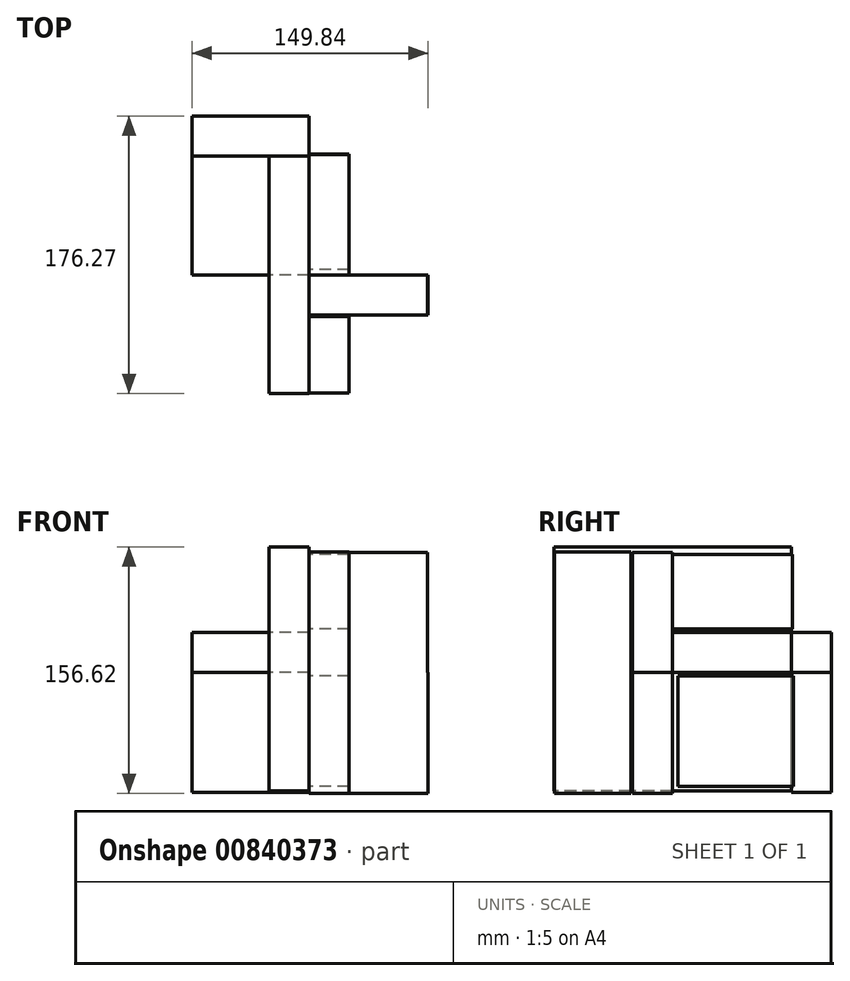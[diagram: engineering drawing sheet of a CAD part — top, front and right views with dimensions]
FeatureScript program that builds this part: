
annotation { "Feature Type Name" : "Feature", "Feature Type Description" : "" }
export const myFeature = defineFeature(function(context is Context, id is Id, definition is map)
    precondition{}
    {
        {
            var Q0;
            Q0=qCreatedBy(makeId("Top.planeOp"),FACE);
            var sketch = newSketch(context, id + "F0", { "sketchPlane" : qUnion([Q0])});
            skLineSegment(sketch, "E0.bottom", {"start": v(0, 0) * mm, "end": v(-74.45, 0) * mm});
            skLineSegment(sketch, "E0.top", {"start": v(0, 75.65) * mm, "end": v(-74.45, 75.65) * mm});
            skLineSegment(sketch, "E0.left", {"start": v(0, 0) * mm, "end": v(0, 75.65) * mm});
            skLineSegment(sketch, "E0.right", {"start": v(-74.45, 0) * mm, "end": v(-74.45, 75.65) * mm});
            skSolve(sketch);
        }
        {
            var Q0;
            Q0=makeQuery(id+"F0.imprint","IMPRINT",FACE,{"disambiguationData":[TD([[makeQuery(id+"F0.imprint","IMPRINT",EDGE,{"derivedFrom":sQuery(id+"F0.wireOp",EDGE,"E0.bottom")}),-1.0]])]});
            extrude(context, id + "F1", {"entities" : qUnion([Q0]), "depth" : 25.4 * mm, "offsetDistance" : 25.4 * mm});
        }
        {
            var Q0;
            Q0=makeQuery(id+"F1.opExtrude","SWEPT_FACE",FACE,{"disambiguationData":[OSD([sQuery(id+"F0.wireOp",EDGE,"E0.top")])]});
            var sketch = newSketch(context, id + "F2", { "sketchPlane" : qUnion([Q0])});
            skSolve(sketch);
        }
        {
            var Q0;
            Q0=makeQuery(id+"F1.opExtrude","SWEPT_FACE",FACE,{"disambiguationData":[OSD([sQuery(id+"F0.wireOp",EDGE,"E0.top")])]});
            var sketch = newSketch(context, id + "F3", { "sketchPlane" : qUnion([Q0])});
            skLineSegment(sketch, "E1.bottom", {"start": v(0, -76.29) * mm, "end": v(74.45, -76.29) * mm});
            skLineSegment(sketch, "E1.top", {"start": v(0, 0) * mm, "end": v(74.45, 0) * mm});
            skLineSegment(sketch, "E1.left", {"start": v(0, -76.29) * mm, "end": v(0, 0) * mm});
            skLineSegment(sketch, "E1.right", {"start": v(74.45, -76.29) * mm, "end": v(74.45, 0) * mm});
            skSolve(sketch);
        }
        {
            var Q0;
            Q0 = qSketchRegion(id + "F3", true);
            extrude(context, id + "F4", {"entities" : qUnion([Q0]), "depth" : 25.4 * mm, "offsetDistance" : 25.4 * mm});
        }
        {
            var Q0;
            {var subQ0=sQuery(id+"F0.wireOp",EDGE,"E0.top");Q0=makeQuery(id+"F2.imprint","IMPRINT",FACE,{"disambiguationData":[TD([[makeQuery(id+"F2.imprint","IMPRINT",EDGE,{"derivedFrom":makeQuery(id+"F1.opExtrude","CAP_EDGE",EDGE,{"disambiguationData":[OSD([subQ0])],"isStart":true})}),1.0]])]});}
            var Q1;
            Q1 = qSketchRegion(id + "F2", true);
            var Q2;
            Q2 = qSketchRegion(id + "F3", true);
            extrude(context, id + "F5", {"entities" : qUnion([Q0, Q1, Q2]), "depth" : 25.4 * mm, "offsetDistance" : 25.4 * mm});
        }
        {
            var Q0;
            Q0=qCreatedBy(makeId("Front.planeOp"),FACE);
            var sketch = newSketch(context, id + "F6", { "sketchPlane" : qUnion([Q0])});
            skLineSegment(sketch, "E2.bottom", {"start": v(0, 0) * mm, "end": v(75.4, 0) * mm});
            skLineSegment(sketch, "E2.top", {"start": v(0, -76.94) * mm, "end": v(75.4, -76.94) * mm});
            skLineSegment(sketch, "E2.left", {"start": v(0, 0) * mm, "end": v(0, -76.94) * mm});
            skLineSegment(sketch, "E2.right", {"start": v(75.4, 0) * mm, "end": v(75.4, -76.94) * mm});
            skLineSegment(sketch, "E3.bottom", {"start": v(0, 0) * mm, "end": v(75.09, 0) * mm});
            skLineSegment(sketch, "E3.top", {"start": v(0, 76.25) * mm, "end": v(75.09, 76.25) * mm});
            skLineSegment(sketch, "E3.left", {"start": v(0, 0) * mm, "end": v(0, 76.25) * mm});
            skLineSegment(sketch, "E3.right", {"start": v(75.09, 0) * mm, "end": v(75.09, 76.25) * mm});
            skSolve(sketch);
        }
        {
            var Q0;
            Q0 = qSketchRegion(id + "F6", true);
            extrude(context, id + "F7", {"entities" : qUnion([Q0]), "depth" : 25.4 * mm, "offsetDistance" : 25.4 * mm});
        }
        {
            var Q0;
            Q0=qCreatedBy(makeId("Right.planeOp"),FACE);
            var sketch = newSketch(context, id + "F8", { "sketchPlane" : qUnion([Q0])});
            skLineSegment(sketch, "E4.bottom", {"start": v(-74.8, 76.6) * mm, "end": v(-26.43, 76.6) * mm});
            skLineSegment(sketch, "E4.top", {"start": v(-74.8, -76.69) * mm, "end": v(-26.43, -76.69) * mm});
            skLineSegment(sketch, "E4.left", {"start": v(-74.8, 76.6) * mm, "end": v(-74.8, -76.69) * mm});
            skLineSegment(sketch, "E4.right", {"start": v(-26.43, 76.6) * mm, "end": v(-26.43, -76.69) * mm});
            skLineSegment(sketch, "E5.bottom", {"start": v(0, 74.79) * mm, "end": v(76.37, 74.79) * mm});
            skLineSegment(sketch, "E5.top", {"start": v(0, 27.62) * mm, "end": v(76.37, 27.62) * mm});
            skLineSegment(sketch, "E5.left", {"start": v(0, 74.79) * mm, "end": v(0, 27.62) * mm});
            skLineSegment(sketch, "E5.right", {"start": v(76.37, 74.79) * mm, "end": v(76.37, 27.62) * mm});
            skLineSegment(sketch, "E6.bottom", {"start": v(3.5, -2.3) * mm, "end": v(76.98, -2.3) * mm});
            skLineSegment(sketch, "E6.top", {"start": v(3.5, -72.45) * mm, "end": v(76.98, -72.45) * mm});
            skLineSegment(sketch, "E6.left", {"start": v(3.5, -2.3) * mm, "end": v(3.5, -72.45) * mm});
            skLineSegment(sketch, "E6.right", {"start": v(76.98, -2.3) * mm, "end": v(76.98, -72.45) * mm});
            skSolve(sketch);
        }
        {
            var Q0;
            Q0 = qSketchRegion(id + "F8", true);
            extrude(context, id + "F9", {"entities" : qUnion([Q0]), "depth" : 25.4 * mm, "offsetDistance" : 25.4 * mm});
        }
        {
            var Q0;
            Q0=makeQuery(id+"F9.opExtrude","CAP_FACE",FACE,{"disambiguationData":[OSD([sQuery(id+"F8.wireOp",EDGE,"E5.bottom"),sQuery(id+"F8.wireOp",EDGE,"E5.top"),sQuery(id+"F8.wireOp",EDGE,"E5.left"),sQuery(id+"F8.wireOp",EDGE,"E5.right")])],"isStart":true});
            var sketch = newSketch(context, id + "F10", { "sketchPlane" : qUnion([Q0])});
            skLineSegment(sketch, "E7.bottom", {"start": v(-75.64, 79.68) * mm, "end": v(75.22, 79.68) * mm});
            skLineSegment(sketch, "E7.top", {"start": v(-75.64, -75.17) * mm, "end": v(75.22, -75.17) * mm});
            skLineSegment(sketch, "E7.left", {"start": v(-75.64, 79.68) * mm, "end": v(-75.64, -75.17) * mm});
            skLineSegment(sketch, "E7.right", {"start": v(75.22, 79.68) * mm, "end": v(75.22, -75.17) * mm});
            skSolve(sketch);
        }
        {
            var Q0;
            Q0 = qSketchRegion(id + "F10", true);
            extrude(context, id + "F11", {"entities" : qUnion([Q0]), "depth" : 25.4 * mm, "offsetDistance" : 25.4 * mm});
        }
    });
